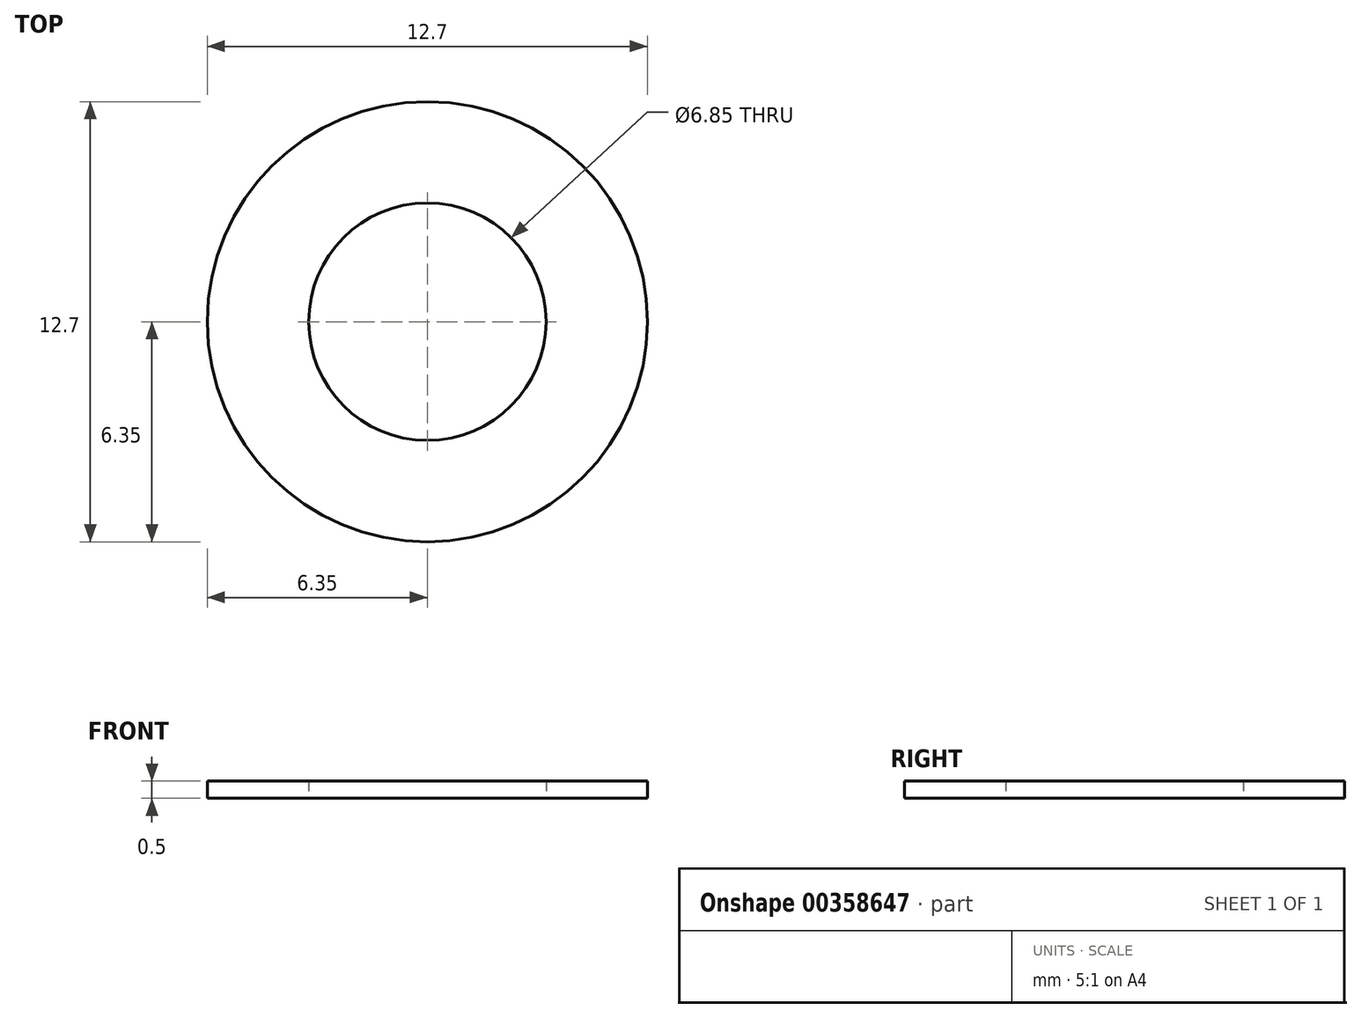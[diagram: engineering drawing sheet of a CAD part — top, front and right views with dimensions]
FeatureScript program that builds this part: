
annotation { "Feature Type Name" : "Feature", "Feature Type Description" : "" }
export const myFeature = defineFeature(function(context is Context, id is Id, definition is map)
    precondition{}
    {
        {
            var Q0;
            Q0=qCreatedBy(makeId("Top.planeOp"),FACE);
            var sketch = newSketch(context, id + "F0", { "sketchPlane" : qUnion([Q0])});
            skCircle(sketch, "E0", {"center": v(0, 0) * mm, "radius": 6.35 * mm});
            skCircle(sketch, "E1", {"center": v(0, 0) * mm, "radius": 3.43 * mm});
            skSolve(sketch);
        }
        {
            var Q0;
            Q0 = qSketchRegion(id + "F0", true);
            extrude(context, id + "F1", {"entities" : qUnion([Q0]), "depth" : .5 * mm, "offsetDistance" : 25 * mm});
        }
    });
